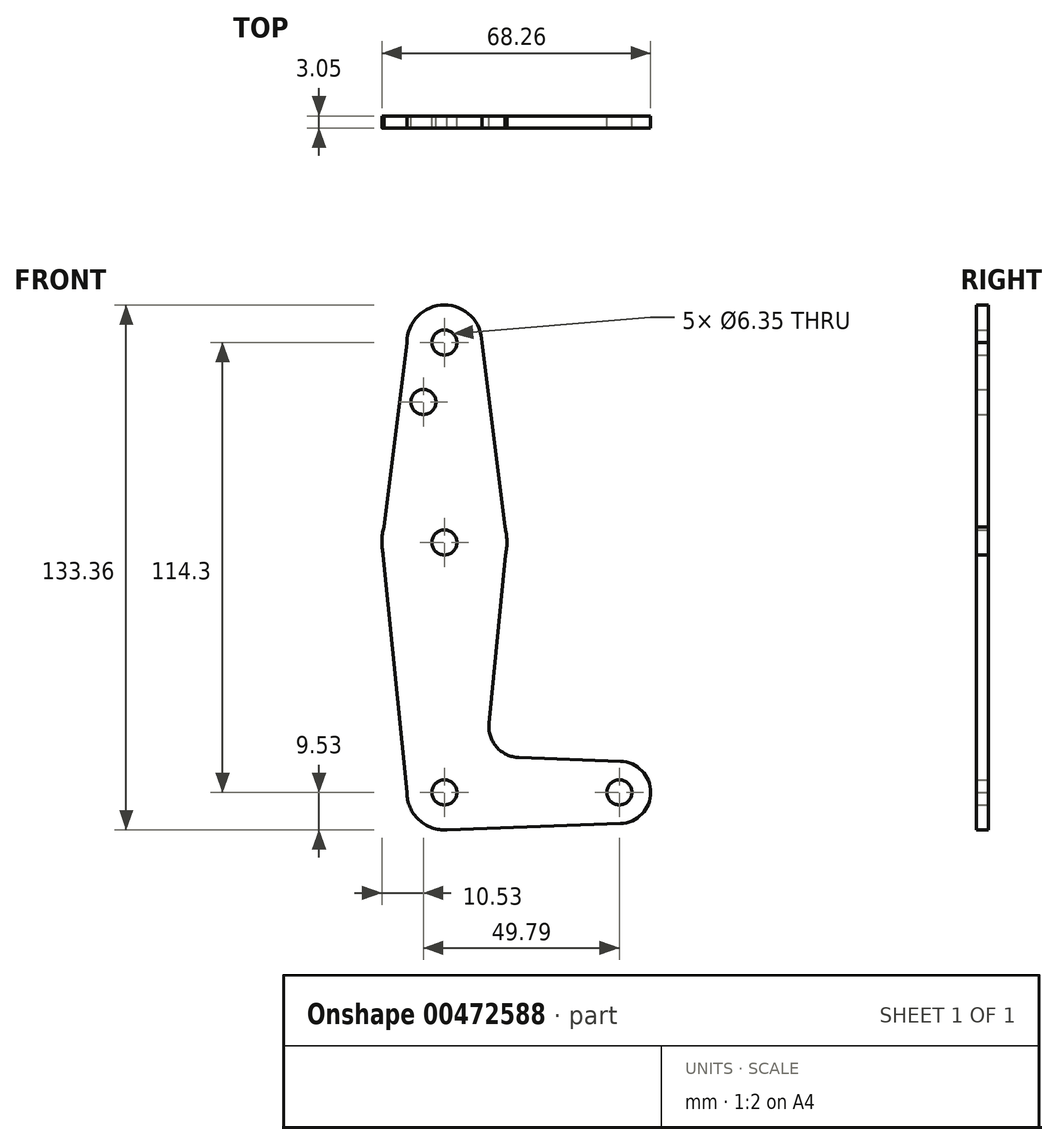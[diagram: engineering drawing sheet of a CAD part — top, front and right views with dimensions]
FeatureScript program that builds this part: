
annotation { "Feature Type Name" : "Feature", "Feature Type Description" : "" }
export const myFeature = defineFeature(function(context is Context, id is Id, definition is map)
    precondition{}
    {
        {
            var Q0;
            Q0=qCreatedBy(makeId("Front.planeOp"),FACE);
            var sketch = newSketch(context, id + "F0", { "sketchPlane" : qUnion([Q0])});
            skLineSegment(sketch, "E0", {"start": v(0, 0) * mm, "end": v(0, 114.3) * mm});
            skLineSegment(sketch, "E1", {"start": v(0, 0) * mm, "end": v(44.45, 0) * mm});
            skCircle(sketch, "E2", {"center": v(0, 114.3) * mm, "radius": 9.53 * mm});
            skCircle(sketch, "E3", {"center": v(0, 63.5) * mm, "radius": 15.88 * mm});
            skCircle(sketch, "E4", {"center": v(0, 0) * mm, "radius": 9.53 * mm});
            skCircle(sketch, "E5", {"center": v(44.45, 0) * mm, "radius": 7.94 * mm});
            skLineSegment(sketch, "E6", {"start": v(0, 63.5) * mm, "end": v(0, 0) * mm});
            skLineSegment(sketch, "E7", {"start": v(-9.52, 114.3) * mm, "end": v(-15.88, 63.5) * mm});
            skLineSegment(sketch, "E8", {"start": v(9.52, 114.3) * mm, "end": v(15.88, 63.5) * mm});
            skLineSegment(sketch, "E9", {"start": v(15.88, 63.5) * mm, "end": v(11.32, 17.58) * mm});
            skLineSegment(sketch, "E10", {"start": v(18.95, 8.85) * mm, "end": v(44.73, 7.93) * mm});
            skCircle(sketch, "E11", {"center": v(0, 114.3) * mm, "radius": 3.18 * mm});
            skCircle(sketch, "E12", {"center": v(-5.34, 99.2) * mm, "radius": 3.18 * mm});
            skCircle(sketch, "E13", {"center": v(0, 63.5) * mm, "radius": 3.18 * mm});
            skCircle(sketch, "E14", {"center": v(0, 0) * mm, "radius": 3.18 * mm});
            skCircle(sketch, "E15", {"center": v(44.45, 0) * mm, "radius": 3.18 * mm});
            skArc(sketch, "E16.filletArc", {"start": v(11.32, 17.58) * mm, "mid": v(13.24, 11.56) * mm, "end": v(18.95, 8.85) * mm});
            skLineSegment(sketch, "E17", {"start": v(0, -9.53) * mm, "end": v(44.73, -7.93) * mm});
            skLineSegment(sketch, "E18", {"start": v(-9.52, 0) * mm, "end": v(-15.88, 63.5) * mm});
            skSolve(sketch);
        }
        {
            var Q0;
            Q0 = qSketchRegion(id + "F0", true);
            var Q1;
            {var subQ0=sQuery(id+"F0.wireOp",EDGE,"E14");var subQ1=sQuery(id+"F0.wireOp",EDGE,"E1");var subQ2=makeQuery(id+"F0.imprint","INTERSECT",VERTEX,{"derivedFrom":[subQ1,subQ0]});Q1=makeQuery(id+"F0.imprint","IMPRINT",FACE,{"disambiguationData":[TD([[makeQuery(id+"F0.imprint","IMPRINT",EDGE,{"disambiguationData":[TD([[subQ2,-1.0]])],"derivedFrom":subQ1}),1.0]])]});}
            extrude(context, id + "F1", {"entities" : qUnion([Q0, Q1]), "depth" : 3.05 * mm});
        }
    });
